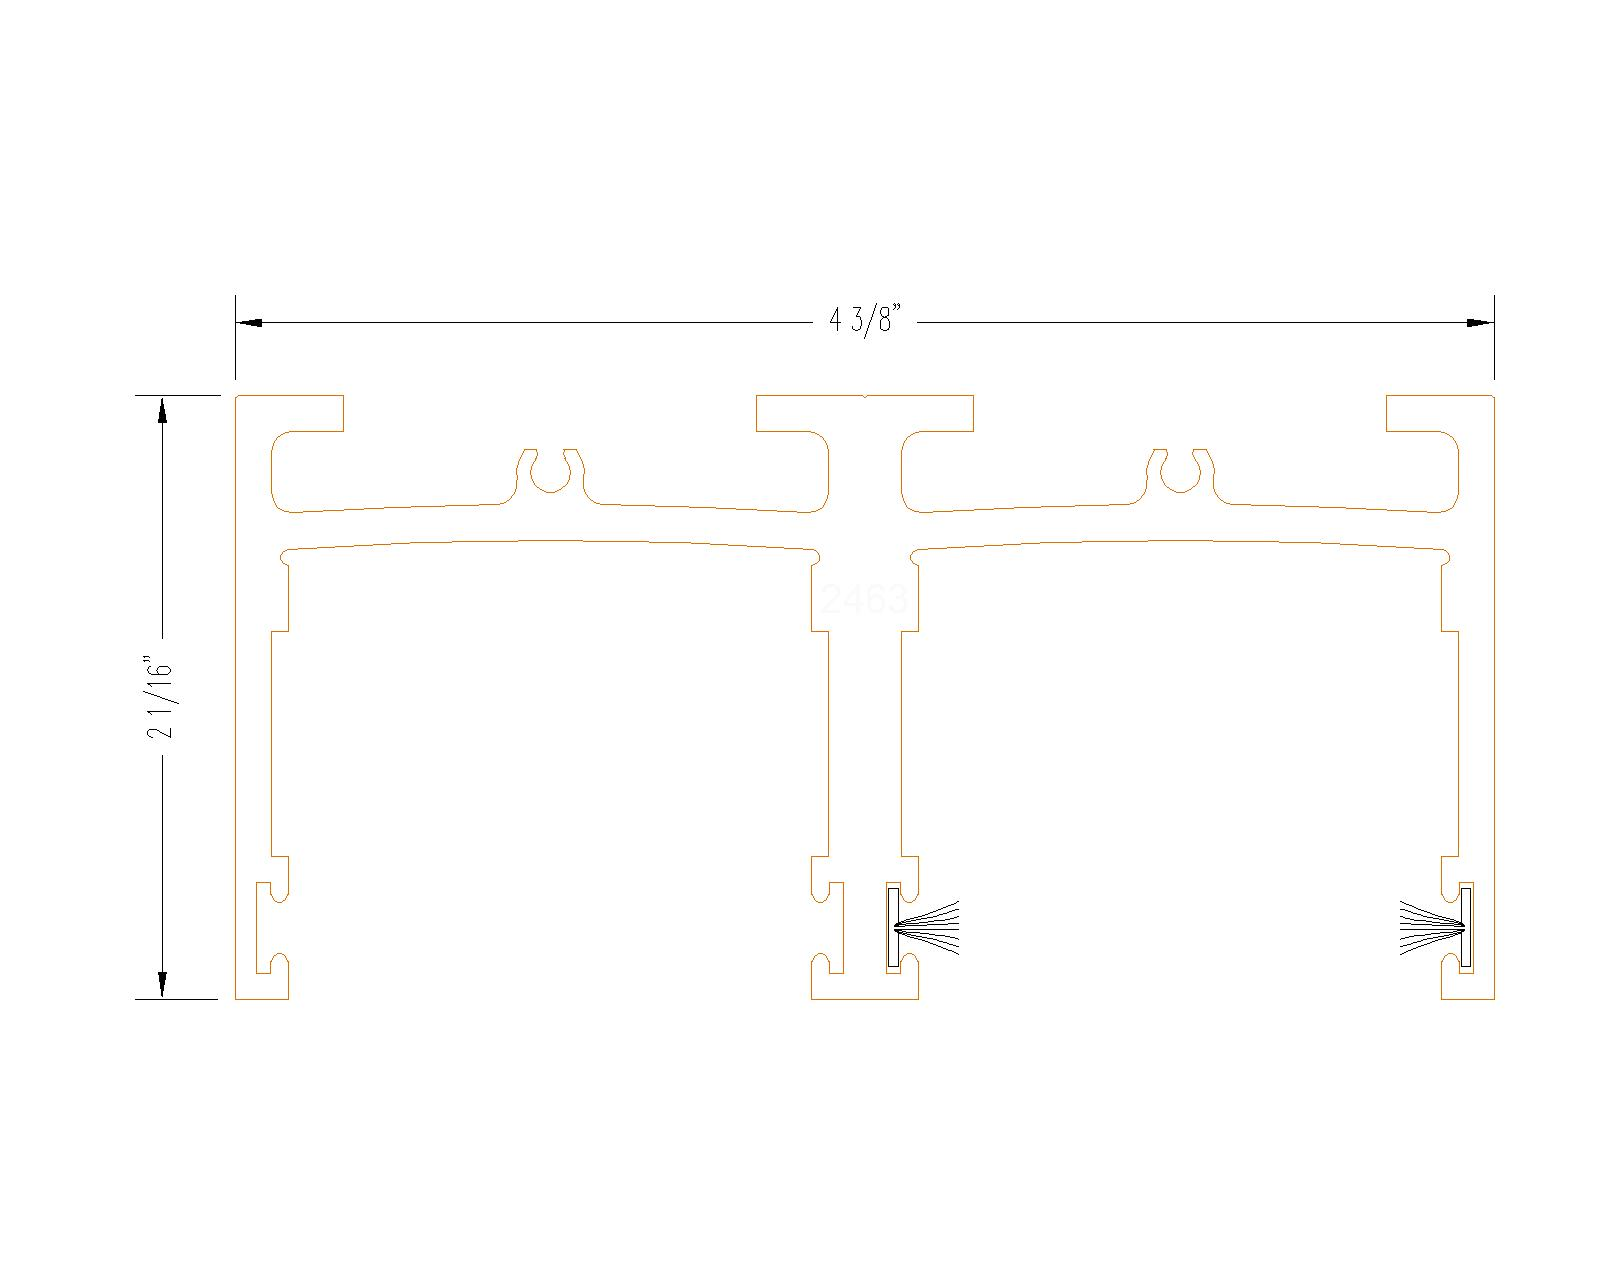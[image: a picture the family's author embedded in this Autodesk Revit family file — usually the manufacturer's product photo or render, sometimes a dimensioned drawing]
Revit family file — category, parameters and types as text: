
# Revit family: PRLMaxSlider_WallSystem
name_source: partatom
category: Puertas
units: mm (PartAtom-declared; Revit-internal decimal feet)

## family parameters
Anfitrión = Muro
Compartido = No
Corte con vacíos al cargar = No
Número OmniClass = 23.30.10.00
Punto de cálculo de habitación = No
Siempre vertical = Sí
Título OmniClass = Doors

## types (1)
- PRLMaxSlider_WallSystem
    Altura = 7' - 0"
    Altura aproximada = 7' - 0"
    Anchura = 15' - 0"
    Anchura aproximada = 15' - 0"
    Cierre de muro = Por anfitrión
    Configurations = PRL Wall System
    Fabricante = PRL
    Frame Projection Ext. = 0' - 1"
    Frame Projection Int. = 0' - 1"
    Frame Width = 0' - 3"
    Glass_Thickness = 1/2"
    H_TopRail_B = 6' - 10 11/32"
    Height = 7' - 0"
    MF2 = PRL MS
    Modelo = Max Slider Wall System
    Number Fixed Panels = 2
    Roller Options = PRL Cancun Series (Bottom Roller)
    TH_SingleFrame = 0' - 2 3/16"
    URL = https://www.prlglass.com
    Width = 15' - 0"
    X01G = 1 1/8"
    X01W = PRL Wall System
    X02G = 1/2"
    X02M = PRL Wall System
    X03G = 1/4"
    X03P = PRL Wall System
    X04B = PRL Wall System
    XCON = PRL Wall System
    XConfig = WallSystem XO (Left) : WallSystem
    XR0 = PRL Cabo Series (Top Hung)
    XR1 = PRL Cancun Series (Bottom Roller)
    XRCON = PRL Cancun Series (Bottom Roller)
    XWSL = WallSystem XO (Left) : WallSystem
    XWSR = WallSystem OX (Right)

## geometry (parser evidence)
native form markers: Sweep x64
no freeform markers — native parametric forms only
